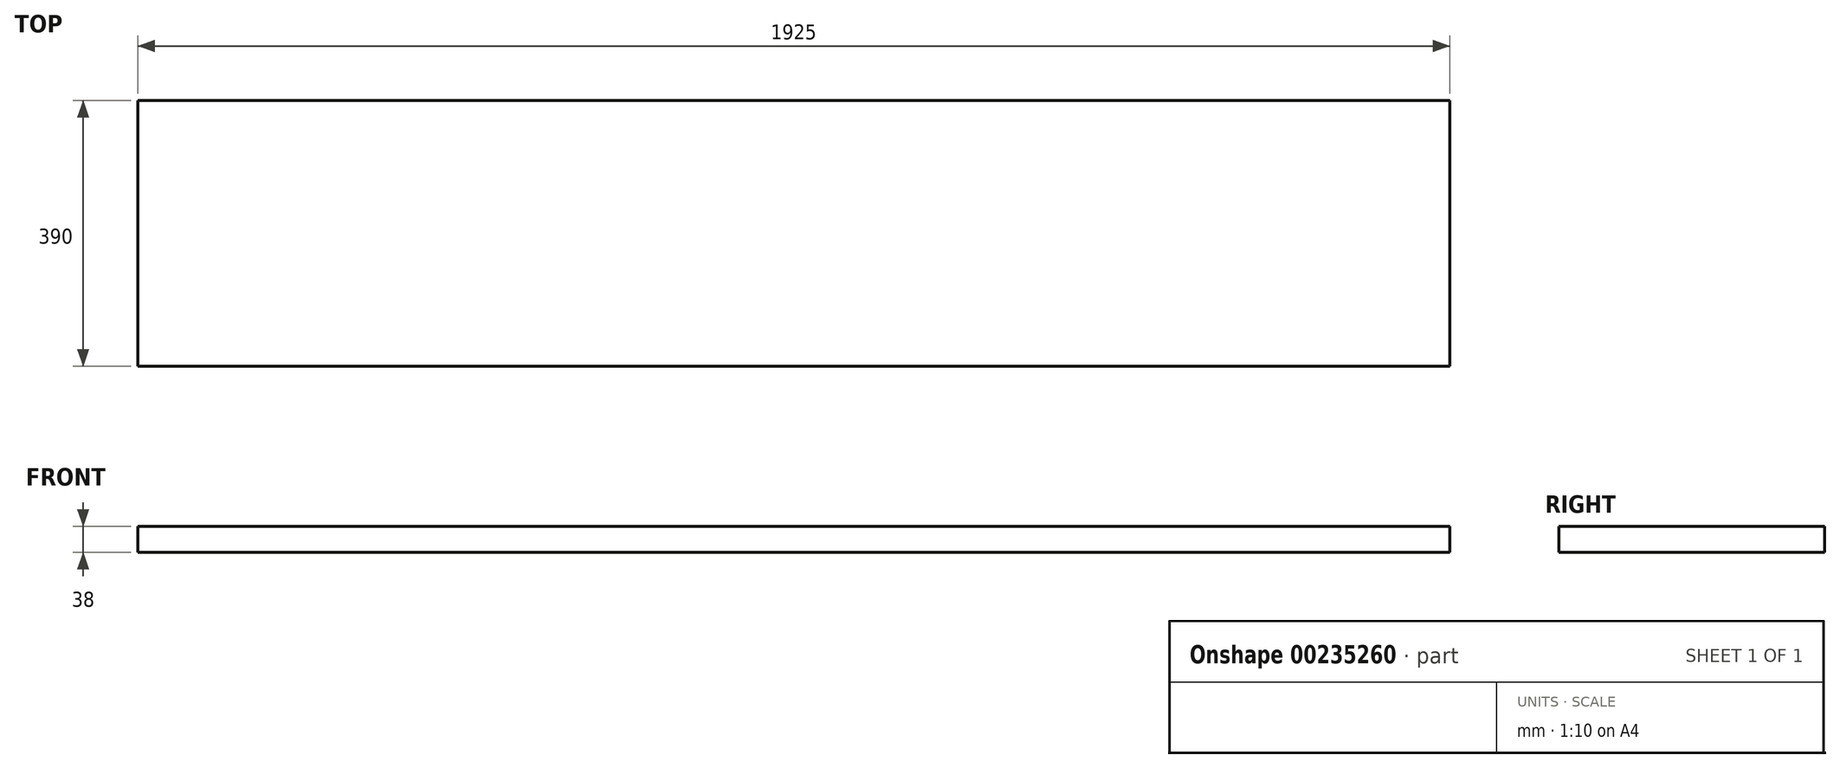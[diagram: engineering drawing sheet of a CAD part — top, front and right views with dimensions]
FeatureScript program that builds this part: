
annotation { "Feature Type Name" : "Feature", "Feature Type Description" : "" }
export const myFeature = defineFeature(function(context is Context, id is Id, definition is map)
    precondition{}
    {
        {
            var Q0;
            Q0=qCreatedBy(makeId("Right.planeOp"),FACE);
            var sketch = newSketch(context, id + "F0", { "sketchPlane" : qUnion([Q0])});
            skLineSegment(sketch, "E0.bottom", {"start": v(0, 832) * mm, "end": v(-390, 832) * mm});
            skLineSegment(sketch, "E0.top", {"start": v(0, 870) * mm, "end": v(-390, 870) * mm});
            skLineSegment(sketch, "E0.left", {"start": v(0, 832) * mm, "end": v(0, 870) * mm});
            skLineSegment(sketch, "E0.right", {"start": v(-390, 832) * mm, "end": v(-390, 870) * mm});
            skSolve(sketch);
        }
        {
            var Q0;
            Q0=makeQuery(id+"F0.imprint","IMPRINT",FACE,{"disambiguationData":[TD([[makeQuery(id+"F0.imprint","IMPRINT",EDGE,{"derivedFrom":sQuery(id+"F0.wireOp",EDGE,"E0.bottom")}),-1.0]])]});
            extrude(context, id + "F1", {"entities" : qUnion([Q0]), "depth" : 1925 * mm});
        }
    });
